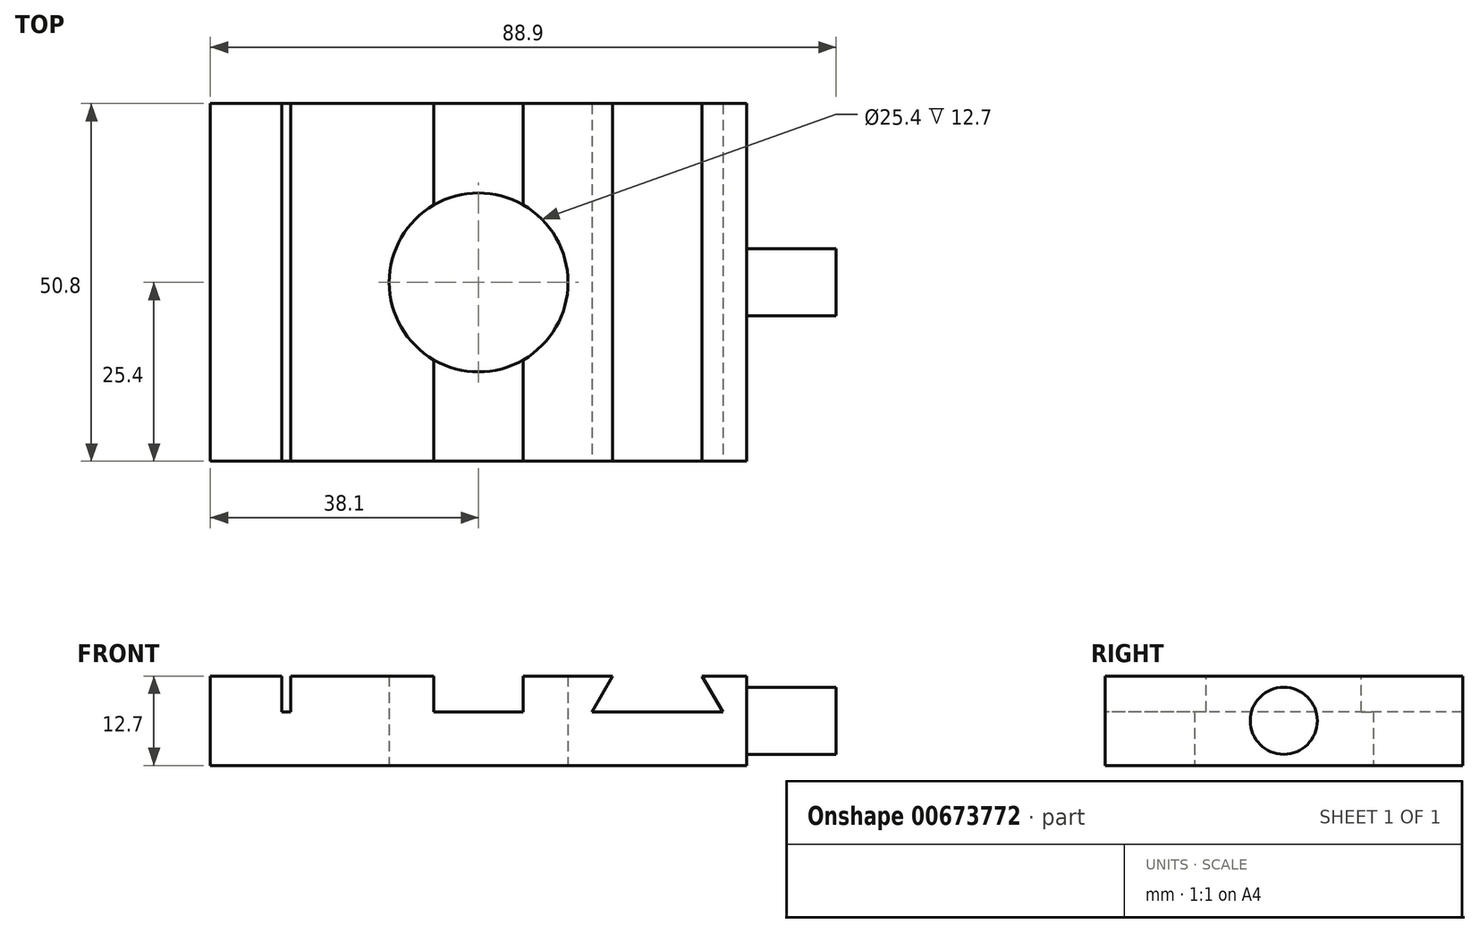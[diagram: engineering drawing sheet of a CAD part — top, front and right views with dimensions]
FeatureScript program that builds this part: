
annotation { "Feature Type Name" : "Feature", "Feature Type Description" : "" }
export const myFeature = defineFeature(function(context is Context, id is Id, definition is map)
    precondition{}
    {
        {
            var Q0;
            Q0=qCreatedBy(makeId("Top.planeOp"),FACE);
            var sketch = newSketch(context, id + "F0", { "sketchPlane" : qUnion([Q0])});
            skLineSegment(sketch, "E0.bottom", {"start": v(38.1, -25.4) * mm, "end": v(-38.1, -25.4) * mm});
            skLineSegment(sketch, "E0.top", {"start": v(38.1, 25.4) * mm, "end": v(-38.1, 25.4) * mm});
            skLineSegment(sketch, "E0.left", {"start": v(38.1, -25.4) * mm, "end": v(38.1, 25.4) * mm});
            skLineSegment(sketch, "E0.right", {"start": v(-38.1, -25.4) * mm, "end": v(-38.1, 25.4) * mm});
            skPoint(sketch, "E0.middle", {"position": v(0, 0) * mm});
            skCircle(sketch, "E1", {"center": v(0, 0) * mm, "radius": 12.7 * mm});
            skSolve(sketch);
        }
        {
            var Q0;
            Q0 = qSketchRegion(id + "F0", true);
            extrude(context, id + "F1", {"entities" : qUnion([Q0]), "depth" : 12.7 * mm, "offsetDistance" : 25.4 * mm});
        }
        {
            var Q0;
            Q0=makeQuery(id+"F1.opExtrude","CAP_FACE",FACE,{"disambiguationData":[OSD([sQuery(id+"F0.wireOp",EDGE,"E0.bottom"),sQuery(id+"F0.wireOp",EDGE,"E0.top"),sQuery(id+"F0.wireOp",EDGE,"E0.left"),sQuery(id+"F0.wireOp",EDGE,"E0.right"),sQuery(id+"F0.wireOp",EDGE,"E1")])],"isStart":false});
            var sketch = newSketch(context, id + "F2", { "sketchPlane" : qUnion([Q0])});
            skLineSegment(sketch, "E2.bottom", {"start": v(-27.94, 25.4) * mm, "end": v(-26.67, 25.4) * mm});
            skLineSegment(sketch, "E2.top", {"start": v(-27.94, -25.4) * mm, "end": v(-26.67, -25.4) * mm});
            skLineSegment(sketch, "E2.left", {"start": v(-27.94, 25.4) * mm, "end": v(-27.94, -25.4) * mm});
            skLineSegment(sketch, "E2.right", {"start": v(-26.67, 25.4) * mm, "end": v(-26.67, -25.4) * mm});
            skLineSegment(sketch, "E3.bottom", {"start": v(-6.35, 25.4) * mm, "end": v(6.35, 25.4) * mm});
            skLineSegment(sketch, "E3.top", {"start": v(-6.35, -25.4) * mm, "end": v(6.35, -25.4) * mm});
            skLineSegment(sketch, "E3.left", {"start": v(-6.35, 25.4) * mm, "end": v(-6.35, -25.4) * mm});
            skLineSegment(sketch, "E3.right", {"start": v(6.35, 25.4) * mm, "end": v(6.35, -25.4) * mm});
            skLineSegment(sketch, "E4", {"start": v(0, 25.4) * mm, "end": v(0, -25.4) * mm, "construction": true});
            skPoint(sketch, "E5", {"position": v(0, 0) * mm});
            skSolve(sketch);
        }
        {
            var Q0;
            {var subQ0=sQuery(id+"F2.wireOp",EDGE,"E3.top");Q0=makeQuery(id+"F2.imprint","IMPRINT",FACE,{"disambiguationData":[TD([[makeQuery(id+"F2.imprint","IMPRINT",EDGE,{"derivedFrom":subQ0}),-1.0]])]});}
            var Q1;
            {var subQ0=sQuery(id+"F2.wireOp",EDGE,"E3.bottom");Q1=makeQuery(id+"F2.imprint","IMPRINT",FACE,{"disambiguationData":[TD([[makeQuery(id+"F2.imprint","IMPRINT",EDGE,{"derivedFrom":subQ0}),1.0]])]});}
            var Q2;
            Q2=makeQuery(id+"F2.imprint","IMPRINT",FACE,{"disambiguationData":[TD([[makeQuery(id+"F2.imprint","IMPRINT",EDGE,{"derivedFrom":sQuery(id+"F2.wireOp",EDGE,"E2.bottom")}),1.0]])]});
            extrude(context, id + "F3", {"entities" : qUnion([Q0, Q1, Q2]), "operationType" : NewBodyOperationType.REMOVE, "oppositeDirection" : true, "depth" : 5.08 * mm, "offsetDistance" : 25.4 * mm});
        }
        {
            var Q0;
            Q0=makeQuery(id+"F1.opExtrude","SWEPT_FACE",FACE,{"disambiguationData":[OSD([sQuery(id+"F0.wireOp",EDGE,"E0.bottom")])]});
            var sketch = newSketch(context, id + "F4", { "sketchPlane" : qUnion([Q0])});
            skLineSegment(sketch, "E6", {"start": v(19.05, 12.7) * mm, "end": v(16.12, 7.62) * mm});
            skLineSegment(sketch, "E7", {"start": v(16.12, 7.62) * mm, "end": v(34.68, 7.62) * mm});
            skLineSegment(sketch, "E8", {"start": v(34.68, 7.62) * mm, "end": v(31.75, 12.7) * mm});
            skLineSegment(sketch, "E9", {"start": v(31.75, 12.7) * mm, "end": v(19.05, 12.7) * mm});
            skLineSegment(sketch, "E10", {"start": v(25.4, 7.62) * mm, "end": v(25.4, 12.7) * mm, "construction": true});
            skSolve(sketch);
        }
        {
            var Q0;
            Q0=makeQuery(id+"F4.imprint","IMPRINT",FACE,{"disambiguationData":[TD([[makeQuery(id+"F4.imprint","IMPRINT",EDGE,{"derivedFrom":sQuery(id+"F4.wireOp",EDGE,"E6")}),1.0]])]});
            extrude(context, id + "F5", {"entities" : qUnion([Q0]), "operationType" : NewBodyOperationType.REMOVE, "endBound" : BoundingType.THROUGH_ALL, "oppositeDirection" : true, "depth" : 25.4 * mm, "offsetDistance" : 25.4 * mm});
        }
        {
            var Q0;
            Q0=makeQuery(id+"F1.opExtrude","SWEPT_FACE",FACE,{"disambiguationData":[OSD([sQuery(id+"F0.wireOp",EDGE,"E0.left")])]});
            var sketch = newSketch(context, id + "F6", { "sketchPlane" : qUnion([Q0])});
            skCircle(sketch, "E11", {"center": v(0, 6.35) * mm, "radius": 4.76 * mm});
            skPoint(sketch, "E11.centerSnap0", {"position": v(-25.4, 6.35) * mm});
            skPoint(sketch, "E11.centerSnap1", {"position": v(0, 12.7) * mm});
            skSolve(sketch);
        }
        {
            var Q0;
            Q0=makeQuery(id+"F6.imprint","IMPRINT",FACE,{"disambiguationData":[TD([[makeQuery(id+"F6.imprint","IMPRINT",EDGE,{"derivedFrom":sQuery(id+"F6.wireOp",EDGE,"E11")}),1.0]])]});
            extrude(context, id + "F7", {"entities" : qUnion([Q0]), "operationType" : NewBodyOperationType.ADD, "depth" : 12.7 * mm, "offsetDistance" : 25.4 * mm});
        }
    });
